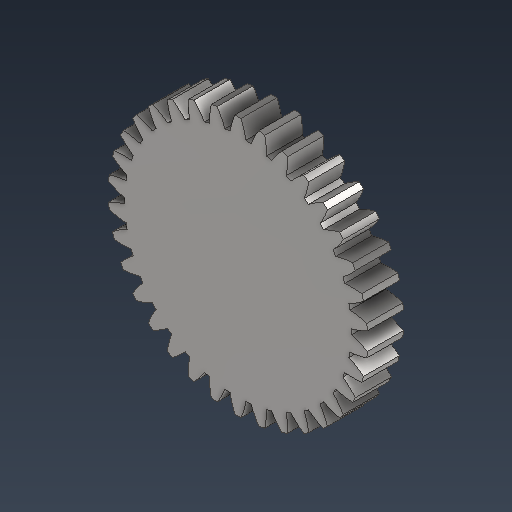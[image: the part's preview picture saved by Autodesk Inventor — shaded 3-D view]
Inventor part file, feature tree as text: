
AUTODESK INVENTOR PART (.ipt)
format: ipt  version: 2021 (Build 250183000, 183)  size: 298,496 bytes
history: native  units: mm (DEFAULTED — no unit token found)
features: plane x3, other x3, sketch x2, extrude x1
ambient origin geometry x8: Origin, YZ Plane, XZ Plane, XY Plane, X Axis, Y Axis, Z Axis, Center Point
bodies: Solid1 (feature_tree)
feature tree (9):
  extrude  "Extrusion1"  Depth=0.5mm TaperAngle=0.0deg
  plane  "Work Plane2"
  plane  "Work Plane8"
  plane  "Work Plane9"
  other  "Engrenagem reta"
  sketch  "Sketch1"  dims[d0=3.6mm d1=0.5mm d2=0.0mm]
  sketch  "Sketch2"  dims[d3=3.4mm d4=10.0mm d5=0.0mm d16=3.0mm d17=0.0mm d34=0.923998mm d39=0.0mm d41=0.0mm d43=3.0mm d46=3.0mm d47=0.0mm d48=0.0mm]
  other  "Srf1"
  other  "Diâmetro do flanco"
